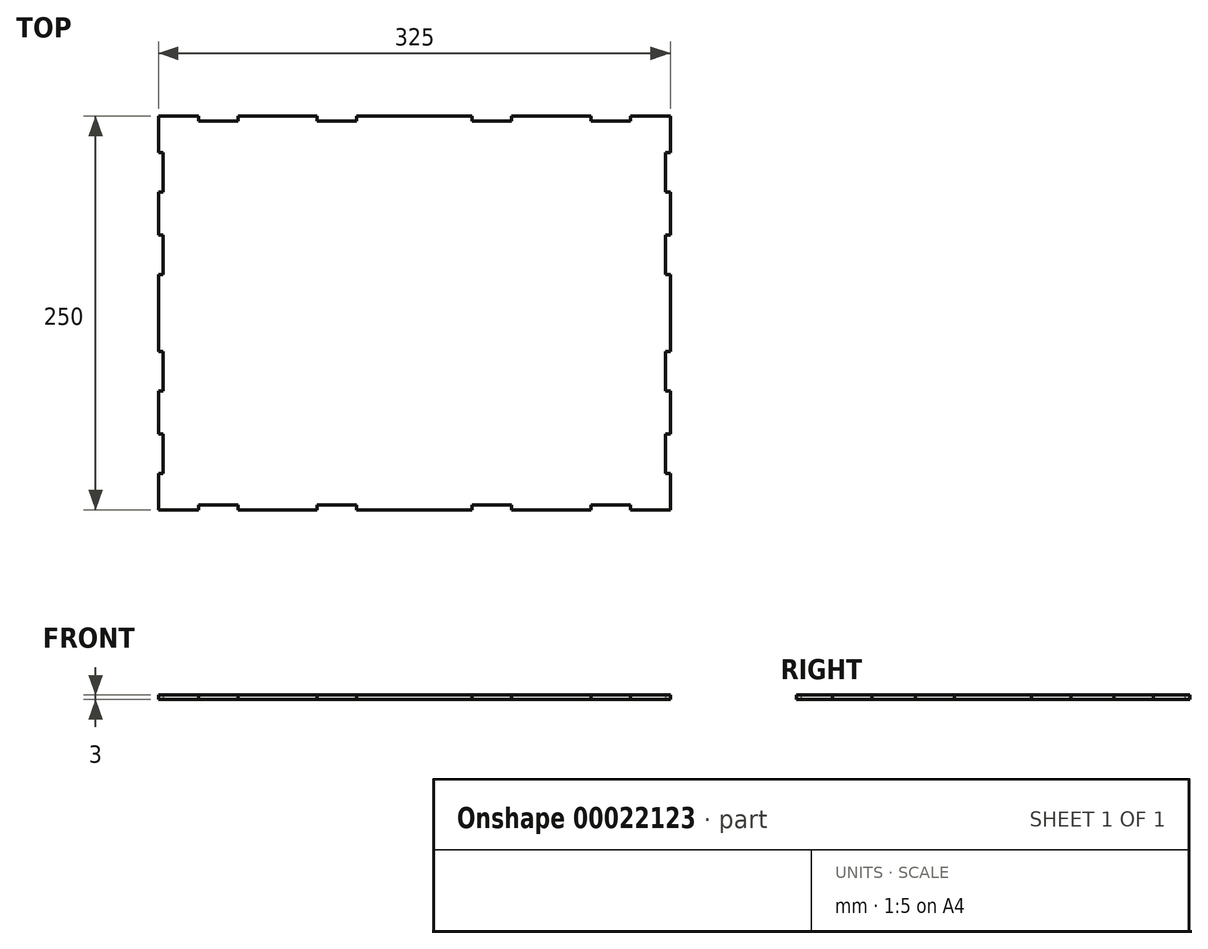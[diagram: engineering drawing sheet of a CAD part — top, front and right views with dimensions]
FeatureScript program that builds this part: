
annotation { "Feature Type Name" : "Feature", "Feature Type Description" : "" }
export const myFeature = defineFeature(function(context is Context, id is Id, definition is map)
    precondition{}
    {
        {
            var Q0;
            Q0=qCreatedBy(makeId("Top.planeOp"),FACE);
            var sketch = newSketch(context, id + "F0", { "sketchPlane" : qUnion([Q0])});
            skLineSegment(sketch, "E0.rect.bottom", {"start": v(162.5, -125) * mm, "end": v(137.13, -125) * mm});
            skLineSegment(sketch, "E0.rect.top", {"start": v(162.5, 125) * mm, "end": v(137.13, 125) * mm});
            skLineSegment(sketch, "E0.rect.left", {"start": v(162.5, -125) * mm, "end": v(162.5, -101.91) * mm});
            skLineSegment(sketch, "E0.rect.right", {"start": v(-162.5, -125) * mm, "end": v(-162.5, -101.91) * mm});
            skPoint(sketch, "E0.rect.middle", {"position": v(0, 0) * mm});
            skLineSegment(sketch, "E1", {"start": v(0, 125) * mm, "end": v(0, -125) * mm, "construction": true});
            skLineSegment(sketch, "E2", {"start": v(162.5, 0) * mm, "end": v(-162.5, 0) * mm, "construction": true});
            skLineSegment(sketch, "E3.top", {"start": v(-137.13, 122) * mm, "end": v(-112.13, 122) * mm});
            skLineSegment(sketch, "E3.left", {"start": v(-137.13, 125) * mm, "end": v(-137.13, 122) * mm});
            skLineSegment(sketch, "E3.right", {"start": v(-112.13, 125) * mm, "end": v(-112.13, 122) * mm});
            skLineSegment(sketch, "E4.top", {"start": v(-61.72, 122) * mm, "end": v(-36.72, 122) * mm});
            skLineSegment(sketch, "E4.left", {"start": v(-61.72, 125) * mm, "end": v(-61.72, 122) * mm});
            skLineSegment(sketch, "E4.right", {"start": v(-36.72, 125) * mm, "end": v(-36.72, 122) * mm});
            skLineSegment(sketch, "E5.MirrorCS", {"start": v(61.72, 122) * mm, "end": v(36.72, 122) * mm});
            skLineSegment(sketch, "E6.MirrorCS", {"start": v(61.72, 125) * mm, "end": v(61.72, 122) * mm});
            skLineSegment(sketch, "E7.MirrorCS", {"start": v(36.72, 125) * mm, "end": v(36.72, 122) * mm});
            skLineSegment(sketch, "E8.MirrorCS", {"start": v(137.13, 122) * mm, "end": v(112.13, 122) * mm});
            skLineSegment(sketch, "E9.MirrorCS", {"start": v(137.13, 125) * mm, "end": v(137.13, 122) * mm});
            skLineSegment(sketch, "E10.MirrorCS", {"start": v(112.13, 125) * mm, "end": v(112.13, 122) * mm});
            skLineSegment(sketch, "E11.trimOffspring", {"start": v(-137.13, 125) * mm, "end": v(-162.5, 125) * mm});
            skLineSegment(sketch, "E12.trimOffspring", {"start": v(36.72, 125) * mm, "end": v(-36.72, 125) * mm});
            skLineSegment(sketch, "E13.trimOffspring", {"start": v(-61.72, 125) * mm, "end": v(-112.13, 125) * mm});
            skLineSegment(sketch, "E14.trimOffspring", {"start": v(112.13, 125) * mm, "end": v(61.72, 125) * mm});
            skLineSegment(sketch, "E15.MirrorCS", {"start": v(-137.13, -122) * mm, "end": v(-112.13, -122) * mm});
            skLineSegment(sketch, "E16.MirrorCS", {"start": v(-61.72, -122) * mm, "end": v(-36.72, -122) * mm});
            skLineSegment(sketch, "E17.MirrorCS", {"start": v(61.72, -122) * mm, "end": v(36.72, -122) * mm});
            skLineSegment(sketch, "E18.MirrorCS", {"start": v(137.13, -122) * mm, "end": v(112.13, -122) * mm});
            skLineSegment(sketch, "E19.MirrorCS", {"start": v(-137.13, -125) * mm, "end": v(-137.13, -122) * mm});
            skLineSegment(sketch, "E20.MirrorCS", {"start": v(-112.13, -125) * mm, "end": v(-112.13, -122) * mm});
            skLineSegment(sketch, "E21.MirrorCS", {"start": v(-61.72, -125) * mm, "end": v(-61.72, -122) * mm});
            skLineSegment(sketch, "E22.MirrorCS", {"start": v(-36.72, -125) * mm, "end": v(-36.72, -122) * mm});
            skLineSegment(sketch, "E23.MirrorCS", {"start": v(36.72, -125) * mm, "end": v(36.72, -122) * mm});
            skLineSegment(sketch, "E24.MirrorCS", {"start": v(61.72, -125) * mm, "end": v(61.72, -122) * mm});
            skLineSegment(sketch, "E25.MirrorCS", {"start": v(112.13, -125) * mm, "end": v(112.13, -122) * mm});
            skLineSegment(sketch, "E26.MirrorCS", {"start": v(137.13, -125) * mm, "end": v(137.13, -122) * mm});
            skLineSegment(sketch, "E27.trimOffspring", {"start": v(-137.13, -125) * mm, "end": v(-162.5, -125) * mm});
            skLineSegment(sketch, "E28.trimOffspring", {"start": v(-61.72, -125) * mm, "end": v(-112.13, -125) * mm});
            skLineSegment(sketch, "E29.trimOffspring", {"start": v(36.72, -125) * mm, "end": v(-36.72, -125) * mm});
            skLineSegment(sketch, "E30.trimOffspring", {"start": v(112.13, -125) * mm, "end": v(61.72, -125) * mm});
            skLineSegment(sketch, "E31.bottom", {"start": v(-162.5, 101.91) * mm, "end": v(-159.5, 101.91) * mm});
            skLineSegment(sketch, "E31.top", {"start": v(-162.5, 76.91) * mm, "end": v(-159.5, 76.91) * mm});
            skLineSegment(sketch, "E31.right", {"start": v(-159.5, 101.91) * mm, "end": v(-159.5, 76.91) * mm});
            skLineSegment(sketch, "E32.bottom", {"start": v(-162.5, 49.42) * mm, "end": v(-159.5, 49.42) * mm});
            skLineSegment(sketch, "E32.top", {"start": v(-162.5, 24.42) * mm, "end": v(-159.5, 24.42) * mm});
            skLineSegment(sketch, "E32.right", {"start": v(-159.5, 49.42) * mm, "end": v(-159.5, 24.42) * mm});
            skLineSegment(sketch, "E33.trimOffspring", {"start": v(-162.5, 101.91) * mm, "end": v(-162.5, 125) * mm});
            skLineSegment(sketch, "E34.trimOffspring", {"start": v(-162.5, 49.42) * mm, "end": v(-162.5, 76.91) * mm});
            skLineSegment(sketch, "E35.MirrorCS", {"start": v(159.5, 101.91) * mm, "end": v(159.5, 76.91) * mm});
            skLineSegment(sketch, "E36.MirrorCS", {"start": v(159.5, 49.42) * mm, "end": v(159.5, 24.42) * mm});
            skLineSegment(sketch, "E37.MirrorCS", {"start": v(162.5, 76.91) * mm, "end": v(159.5, 76.91) * mm});
            skLineSegment(sketch, "E38.MirrorCS", {"start": v(162.5, 101.91) * mm, "end": v(159.5, 101.91) * mm});
            skLineSegment(sketch, "E39.MirrorCS", {"start": v(162.5, 49.42) * mm, "end": v(159.5, 49.42) * mm});
            skLineSegment(sketch, "E40.MirrorCS", {"start": v(162.5, 24.42) * mm, "end": v(159.5, 24.42) * mm});
            skLineSegment(sketch, "E41.trimOffspring", {"start": v(162.5, 101.91) * mm, "end": v(162.5, 125) * mm});
            skLineSegment(sketch, "E42.trimOffspring", {"start": v(162.5, 49.42) * mm, "end": v(162.5, 76.91) * mm});
            skLineSegment(sketch, "E43.MirrorCS", {"start": v(-159.5, -49.42) * mm, "end": v(-159.5, -24.42) * mm});
            skLineSegment(sketch, "E44.MirrorCS", {"start": v(-159.5, -101.91) * mm, "end": v(-159.5, -76.91) * mm});
            skLineSegment(sketch, "E45.MirrorCS", {"start": v(159.5, -101.91) * mm, "end": v(159.5, -76.91) * mm});
            skLineSegment(sketch, "E46.MirrorCS", {"start": v(159.5, -49.42) * mm, "end": v(159.5, -24.42) * mm});
            skLineSegment(sketch, "E47.MirrorCS", {"start": v(-162.5, -49.42) * mm, "end": v(-159.5, -49.42) * mm});
            skLineSegment(sketch, "E48.MirrorCS", {"start": v(-162.5, -24.42) * mm, "end": v(-159.5, -24.42) * mm});
            skLineSegment(sketch, "E49.MirrorCS", {"start": v(-162.5, -76.91) * mm, "end": v(-159.5, -76.91) * mm});
            skLineSegment(sketch, "E50.MirrorCS", {"start": v(-162.5, -101.91) * mm, "end": v(-159.5, -101.91) * mm});
            skLineSegment(sketch, "E51.MirrorCS", {"start": v(162.5, -76.91) * mm, "end": v(159.5, -76.91) * mm});
            skLineSegment(sketch, "E52.MirrorCS", {"start": v(162.5, -49.42) * mm, "end": v(159.5, -49.42) * mm});
            skLineSegment(sketch, "E53.MirrorCS", {"start": v(162.5, -24.42) * mm, "end": v(159.5, -24.42) * mm});
            skLineSegment(sketch, "E54.MirrorCS", {"start": v(162.5, -101.91) * mm, "end": v(159.5, -101.91) * mm});
            skLineSegment(sketch, "E55.trimOffspring", {"start": v(162.5, -24.42) * mm, "end": v(162.5, 24.42) * mm});
            skLineSegment(sketch, "E56.trimOffspring", {"start": v(162.5, -76.91) * mm, "end": v(162.5, -49.42) * mm});
            skLineSegment(sketch, "E57.trimOffspring", {"start": v(-162.5, -24.42) * mm, "end": v(-162.5, 24.42) * mm});
            skLineSegment(sketch, "E58.trimOffspring", {"start": v(-162.5, -76.91) * mm, "end": v(-162.5, -49.42) * mm});
            skSolve(sketch);
        }
        {
            var Q0;
            Q0=makeQuery(id+"F0.imprint","IMPRINT",FACE,{"disambiguationData":[TD([[makeQuery(id+"F0.imprint","IMPRINT",EDGE,{"derivedFrom":sQuery(id+"F0.wireOp",EDGE,"E0.rect.bottom")}),-1.0]])]});
            extrude(context, id + "F1", {"entities" : qUnion([Q0]), "depth" : 3 * mm});
        }
    });
